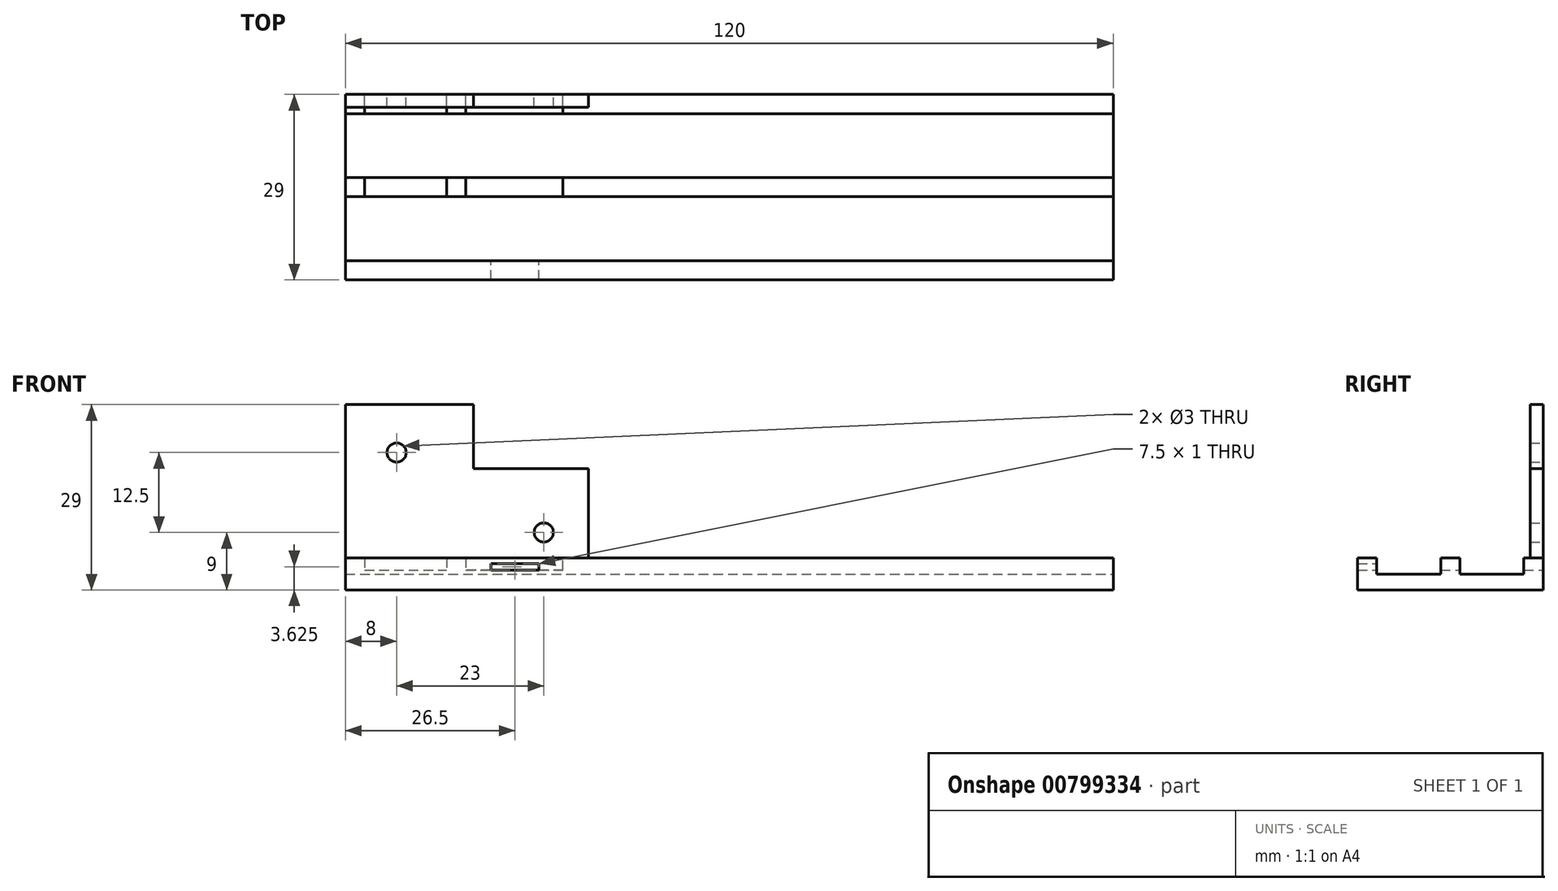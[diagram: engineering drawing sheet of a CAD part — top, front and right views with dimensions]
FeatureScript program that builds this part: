
annotation { "Feature Type Name" : "Feature", "Feature Type Description" : "" }
export const myFeature = defineFeature(function(context is Context, id is Id, definition is map)
    precondition{}
    {
        {
            var Q0;
            Q0=qCreatedBy(makeId("Top.planeOp"),FACE);
            var sketch = newSketch(context, id + "F0", { "sketchPlane" : qUnion([Q0])});
            skLineSegment(sketch, "E0.bottom", {"start": v(-65.83, 15.47) * mm, "end": v(54.17, 15.47) * mm});
            skLineSegment(sketch, "E0.top", {"start": v(-65.83, -13.53) * mm, "end": v(54.17, -13.53) * mm});
            skLineSegment(sketch, "E0.left", {"start": v(-65.83, 15.47) * mm, "end": v(-65.83, -13.53) * mm});
            skLineSegment(sketch, "E0.right", {"start": v(54.17, 15.47) * mm, "end": v(54.17, -13.53) * mm});
            skSolve(sketch);
        }
        {
            var Q0;
            Q0 = qSketchRegion(id + "F0", true);
            extrude(context, id + "F1", {"entities" : qUnion([Q0]), "depth" : 5 * mm, "offsetDistance" : 25 * mm});
        }
        {
            var Q0;
            Q0=makeQuery(id+"F1.opExtrude","CAP_FACE",FACE,{"disambiguationData":[OSD([sQuery(id+"F0.wireOp",EDGE,"E0.bottom"),sQuery(id+"F0.wireOp",EDGE,"E0.top"),sQuery(id+"F0.wireOp",EDGE,"E0.left"),sQuery(id+"F0.wireOp",EDGE,"E0.right")])],"isStart":false});
            var sketch = newSketch(context, id + "F2", { "sketchPlane" : qUnion([Q0])});
            skLineSegment(sketch, "E1.bottom", {"start": v(-65.83, 12.47) * mm, "end": v(54.17, 12.47) * mm});
            skLineSegment(sketch, "E1.top", {"start": v(-65.83, 2.47) * mm, "end": v(54.17, 2.47) * mm});
            skLineSegment(sketch, "E1.left", {"start": v(-65.83, 12.47) * mm, "end": v(-65.83, 2.47) * mm});
            skLineSegment(sketch, "E1.right", {"start": v(54.17, 12.47) * mm, "end": v(54.17, 2.47) * mm});
            skLineSegment(sketch, "E2.bottom", {"start": v(-65.83, -10.53) * mm, "end": v(54.17, -10.53) * mm});
            skLineSegment(sketch, "E2.top", {"start": v(-65.83, -0.53) * mm, "end": v(54.17, -0.53) * mm});
            skLineSegment(sketch, "E2.left", {"start": v(-65.83, -10.53) * mm, "end": v(-65.83, -0.53) * mm});
            skLineSegment(sketch, "E2.right", {"start": v(54.17, -10.53) * mm, "end": v(54.17, -0.53) * mm});
            skSolve(sketch);
        }
        {
            var Q0;
            Q0 = qSketchRegion(id + "F2", true);
            extrude(context, id + "F3", {"entities" : qUnion([Q0]), "operationType" : NewBodyOperationType.REMOVE, "oppositeDirection" : true, "depth" : 2.5 * mm, "offsetDistance" : 25 * mm});
        }
        {
            var Q0;
            Q0=makeQuery(id+"F1.opExtrude","SWEPT_FACE",FACE,{"disambiguationData":[OSD([sQuery(id+"F0.wireOp",EDGE,"E0.bottom")])]});
            var sketch = newSketch(context, id + "F4", { "sketchPlane" : qUnion([Q0])});
            skLineSegment(sketch, "E3.bottom", {"start": v(65.83, 5) * mm, "end": v(45.83, 5) * mm});
            skLineSegment(sketch, "E3.top", {"start": v(65.83, 29) * mm, "end": v(45.83, 29) * mm});
            skLineSegment(sketch, "E3.left", {"start": v(65.83, 5) * mm, "end": v(65.83, 29) * mm});
            skLineSegment(sketch, "E3.right", {"start": v(45.83, 19) * mm, "end": v(45.83, 29) * mm});
            skLineSegment(sketch, "E4.bottom", {"start": v(45.83, 5) * mm, "end": v(27.83, 5) * mm});
            skLineSegment(sketch, "E4.top", {"start": v(45.83, 19) * mm, "end": v(27.83, 19) * mm});
            skLineSegment(sketch, "E4.right", {"start": v(27.83, 5) * mm, "end": v(27.83, 19) * mm});
            skSolve(sketch);
        }
        {
            var Q0;
            Q0 = qSketchRegion(id + "F4", true);
            extrude(context, id + "F5", {"entities" : qUnion([Q0]), "operationType" : NewBodyOperationType.ADD, "oppositeDirection" : true, "depth" : 2 * mm, "offsetDistance" : 25 * mm});
        }
        {
            var Q0;
            Q0=makeQuery(id+"F5.boolean.opBoolean","MERGE",FACE,{"derivedFrom":[makeQuery(id+"F1.opExtrude","SWEPT_FACE",FACE,{"disambiguationData":[OSD([sQuery(id+"F0.wireOp",EDGE,"E0.bottom")])]}),makeQuery(id+"F5.opExtrude","CAP_FACE",FACE,{"disambiguationData":[OSD([sQuery(id+"F4.wireOp",EDGE,"E3.bottom"),sQuery(id+"F4.wireOp",EDGE,"E3.top"),sQuery(id+"F4.wireOp",EDGE,"E3.left"),sQuery(id+"F4.wireOp",EDGE,"E3.right"),sQuery(id+"F4.wireOp",EDGE,"E4.bottom"),sQuery(id+"F4.wireOp",EDGE,"E4.top"),sQuery(id+"F4.wireOp",EDGE,"E4.right")])],"isStart":true})]});
            var sketch = newSketch(context, id + "F6", { "sketchPlane" : qUnion([Q0])});
            skCircle(sketch, "E5", {"center": v(57.83, 21.5) * mm, "radius": 1.5 * mm});
            skCircle(sketch, "E6", {"center": v(34.83, 9) * mm, "radius": 1.5 * mm});
            skSolve(sketch);
        }
        {
            var Q0;
            Q0 = qSketchRegion(id + "F6", true);
            extrude(context, id + "F7", {"entities" : qUnion([Q0]), "operationType" : NewBodyOperationType.REMOVE, "oppositeDirection" : true, "depth" : 25 * mm, "offsetDistance" : 25 * mm});
        }
        {
            var Q0;
            Q0=makeQuery(id+"F5.boolean.opBoolean","MERGE",FACE,{"derivedFrom":[makeQuery(id+"F1.opExtrude","SWEPT_FACE",FACE,{"disambiguationData":[OSD([sQuery(id+"F0.wireOp",EDGE,"E0.bottom")])]}),makeQuery(id+"F5.opExtrude","CAP_FACE",FACE,{"disambiguationData":[OSD([sQuery(id+"F4.wireOp",EDGE,"E3.bottom"),sQuery(id+"F4.wireOp",EDGE,"E3.top"),sQuery(id+"F4.wireOp",EDGE,"E3.left"),sQuery(id+"F4.wireOp",EDGE,"E3.right"),sQuery(id+"F4.wireOp",EDGE,"E4.bottom"),sQuery(id+"F4.wireOp",EDGE,"E4.top"),sQuery(id+"F4.wireOp",EDGE,"E4.right")])],"isStart":true})]});
            var sketch = newSketch(context, id + "F8", { "sketchPlane" : qUnion([Q0])});
            skLineSegment(sketch, "E7.bottom", {"start": v(65.83, 3.13) * mm, "end": v(31.83, 3.12) * mm});
            skLineSegment(sketch, "E7.top", {"start": v(65.83, 5) * mm, "end": v(31.83, 5) * mm});
            skLineSegment(sketch, "E7.right", {"start": v(31.83, 3.12) * mm, "end": v(31.83, 5) * mm});
            skLineSegment(sketch, "E8", {"start": v(62.83, 5) * mm, "end": v(62.83, 3.13) * mm});
            skLineSegment(sketch, "E9", {"start": v(47.03, 5) * mm, "end": v(47.03, 3.12) * mm});
            skLineSegment(sketch, "E10", {"start": v(50.03, 5) * mm, "end": v(50.03, 3.12) * mm});
            skSolve(sketch);
        }
        {
            var Q0;
            {var subQ0=sQuery(id+"F8.wireOp",EDGE,"E7.right");Q0=makeQuery(id+"F8.imprint","IMPRINT",FACE,{"disambiguationData":[TD([[makeQuery(id+"F8.imprint","IMPRINT",EDGE,{"derivedFrom":subQ0}),-1.0]])]});}
            var Q1;
            {var subQ0=sQuery(id+"F8.wireOp",EDGE,"E8");Q1=makeQuery(id+"F8.imprint","IMPRINT",FACE,{"disambiguationData":[TD([[makeQuery(id+"F8.imprint","IMPRINT",EDGE,{"derivedFrom":subQ0}),-1.0]])]});}
            extrude(context, id + "F9", {"entities" : qUnion([Q0, Q1]), "operationType" : NewBodyOperationType.REMOVE, "oppositeDirection" : true, "depth" : 18 * mm, "offsetDistance" : 25 * mm});
        }
        {
            var Q0;
            Q0=makeQuery(id+"F3.boolean.opBoolean","COPY",FACE,{"derivedFrom":makeQuery(id+"F3.opExtrude","SWEPT_FACE",FACE,{"disambiguationData":[OSD([sQuery(id+"F2.wireOp",EDGE,"E2.bottom")])]})});
            var sketch = newSketch(context, id + "F10", { "sketchPlane" : qUnion([Q0])});
            skLineSegment(sketch, "E11.bottom", {"start": v(35.58, 3.12) * mm, "end": v(43.08, 3.12) * mm});
            skLineSegment(sketch, "E11.top", {"start": v(35.58, 4.12) * mm, "end": v(43.08, 4.12) * mm});
            skLineSegment(sketch, "E11.left", {"start": v(35.58, 3.12) * mm, "end": v(35.58, 4.12) * mm});
            skLineSegment(sketch, "E11.right", {"start": v(43.08, 3.12) * mm, "end": v(43.08, 4.12) * mm});
            skSolve(sketch);
        }
        {
            var Q0;
            Q0=makeQuery(id+"F10.imprint","IMPRINT",FACE,{"disambiguationData":[TD([[makeQuery(id+"F10.imprint","IMPRINT",EDGE,{"derivedFrom":sQuery(id+"F10.wireOp",EDGE,"E11.bottom")}),1.0]])]});
            extrude(context, id + "F11", {"entities" : qUnion([Q0]), "operationType" : NewBodyOperationType.REMOVE, "endBound" : BoundingType.THROUGH_ALL, "oppositeDirection" : true, "depth" : 25 * mm, "offsetDistance" : 25 * mm});
        }
    });
